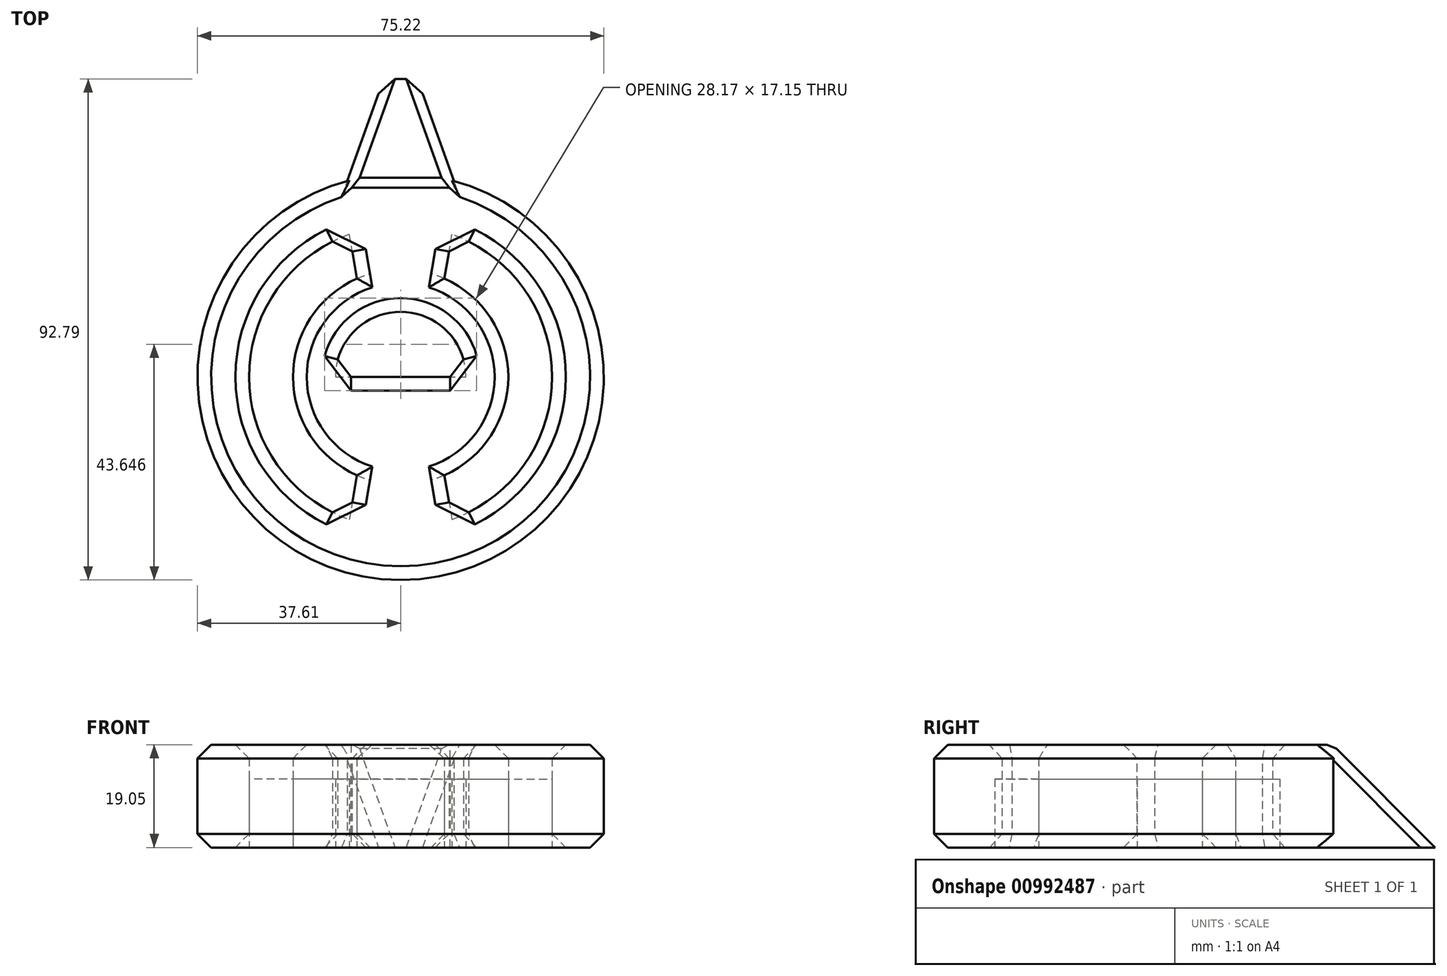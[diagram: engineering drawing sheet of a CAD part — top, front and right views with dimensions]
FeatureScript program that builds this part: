
annotation { "Feature Type Name" : "Feature", "Feature Type Description" : "" }
export const myFeature = defineFeature(function(context is Context, id is Id, definition is map)
    precondition{}
    {
        {
            var Q0;
            Q0=qCreatedBy(makeId("Top.planeOp"),FACE);
            var sketch = newSketch(context, id + "F0", { "sketchPlane" : qUnion([Q0])});
            skLineSegment(sketch, "E0", {"start": v(0, 76.84) * mm, "end": v(0, -76.6) * mm});
            skCircle(sketch, "E1", {"center": v(0, 0) * mm, "radius": 5.51 * mm});
            skCircle(sketch, "E2", {"center": v(0, 0) * mm, "radius": 12.07 * mm});
            skCircle(sketch, "E3", {"center": v(0, 0) * mm, "radius": 37.6 * mm});
            skCircle(sketch, "E4", {"center": v(0, 0) * mm, "radius": 28.06 * mm});
            skCircle(sketch, "E5", {"center": v(0, 0) * mm, "radius": 19.94 * mm});
            skLineSegment(sketch, "E6", {"start": v(-8.1, 18.22) * mm, "end": v(-9.51, 26.4) * mm});
            skLineSegment(sketch, "E7", {"start": v(-76.36, 0) * mm, "end": v(76.42, 0) * mm});
            skLineSegment(sketch, "E8.MirrorCS", {"start": v(-8.1, -18.22) * mm, "end": v(-9.51, -26.4) * mm});
            skLineSegment(sketch, "E9.MirrorCS", {"start": v(8.1, 18.22) * mm, "end": v(9.51, 26.4) * mm});
            skLineSegment(sketch, "E10.MirrorCS", {"start": v(8.1, -18.22) * mm, "end": v(9.51, -26.4) * mm});
            skLineSegment(sketch, "E11", {"start": v(-9.86, 36.3) * mm, "end": v(-3.1, 55.18) * mm});
            skLineSegment(sketch, "E12", {"start": v(-3.1, 55.18) * mm, "end": v(0, 55.18) * mm});
            skLineSegment(sketch, "E13.MirrorCS", {"start": v(9.86, 36.3) * mm, "end": v(3.1, 55.18) * mm});
            skLineSegment(sketch, "E14.MirrorCS", {"start": v(3.1, 55.18) * mm, "end": v(0, 55.18) * mm});
            skSolve(sketch);
        }
        {
            var Q0;
            {var subQ0=sQuery(id+"F0.wireOp",EDGE,"E7");var subQ1=sQuery(id+"F0.wireOp",EDGE,"E0");var subQ2=makeQuery(id+"F0.imprint","INTERSECT",VERTEX,{"derivedFrom":[subQ1,subQ0]});Q0=makeQuery(id+"F0.imprint","IMPRINT",FACE,{"disambiguationData":[TD([[makeQuery(id+"F0.imprint","IMPRINT",EDGE,{"disambiguationData":[TD([[subQ2,-1.0]])],"derivedFrom":subQ1}),1.0]])]});}
            var Q1;
            {var subQ0=sQuery(id+"F0.wireOp",EDGE,"E7");var subQ1=sQuery(id+"F0.wireOp",EDGE,"E0");var subQ2=makeQuery(id+"F0.imprint","INTERSECT",VERTEX,{"derivedFrom":[subQ1,subQ0]});Q1=makeQuery(id+"F0.imprint","IMPRINT",FACE,{"disambiguationData":[TD([[makeQuery(id+"F0.imprint","IMPRINT",EDGE,{"disambiguationData":[TD([[subQ2,-1.0]])],"derivedFrom":subQ1}),-1.0]])]});}
            var Q2;
            {var subQ0=sQuery(id+"F0.wireOp",EDGE,"E1");var subQ1=sQuery(id+"F0.wireOp",EDGE,"E0");var subQ2=makeQuery(id+"F0.imprint","INTERSECT",VERTEX,{"disambiguationData":[OD(0.0)],"derivedFrom":[subQ1,subQ0]});Q2=makeQuery(id+"F0.imprint","IMPRINT",FACE,{"disambiguationData":[TD([[makeQuery(id+"F0.imprint","IMPRINT",EDGE,{"disambiguationData":[TD([[subQ2,-1.0]])],"derivedFrom":subQ1}),-1.0]])]});}
            var Q3;
            {var subQ0=sQuery(id+"F0.wireOp",EDGE,"E1");var subQ1=sQuery(id+"F0.wireOp",EDGE,"E0");var subQ2=makeQuery(id+"F0.imprint","INTERSECT",VERTEX,{"disambiguationData":[OD(0.0)],"derivedFrom":[subQ1,subQ0]});Q3=makeQuery(id+"F0.imprint","IMPRINT",FACE,{"disambiguationData":[TD([[makeQuery(id+"F0.imprint","IMPRINT",EDGE,{"disambiguationData":[TD([[subQ2,-1.0]])],"derivedFrom":subQ1}),1.0]])]});}
            var Q4;
            {var subQ0=sQuery(id+"F0.wireOp",EDGE,"E5");var subQ2=sQuery(id+"F0.wireOp",EDGE,"E0");var subQ3=makeQuery(id+"F0.imprint","INTERSECT",VERTEX,{"disambiguationData":[OD(0.0)],"derivedFrom":[subQ2,subQ0]});Q4=makeQuery(id+"F0.imprint","IMPRINT",FACE,{"disambiguationData":[TD([[makeQuery(id+"F0.imprint","IMPRINT",EDGE,{"disambiguationData":[TD([[subQ3,-1.0]])],"derivedFrom":subQ2}),-1.0]])]});}
            var Q5;
            {var subQ4=sQuery(id+"F0.wireOp",EDGE,"E2");var subQ5=sQuery(id+"F0.wireOp",EDGE,"E0");var subQ6=makeQuery(id+"F0.imprint","INTERSECT",VERTEX,{"disambiguationData":[OD(1.0)],"derivedFrom":[subQ5,subQ4]});Q5=makeQuery(id+"F0.imprint","IMPRINT",FACE,{"disambiguationData":[TD([[makeQuery(id+"F0.imprint","IMPRINT",EDGE,{"disambiguationData":[TD([[subQ6,-1.0]])],"derivedFrom":subQ5}),-1.0]])]});}
            var Q6;
            {var subQ4=sQuery(id+"F0.wireOp",EDGE,"E2");var subQ5=sQuery(id+"F0.wireOp",EDGE,"E0");var subQ6=makeQuery(id+"F0.imprint","INTERSECT",VERTEX,{"disambiguationData":[OD(1.0)],"derivedFrom":[subQ5,subQ4]});Q6=makeQuery(id+"F0.imprint","IMPRINT",FACE,{"disambiguationData":[TD([[makeQuery(id+"F0.imprint","IMPRINT",EDGE,{"disambiguationData":[TD([[subQ6,-1.0]])],"derivedFrom":subQ5}),1.0]])]});}
            var Q7;
            {var subQ0=sQuery(id+"F0.wireOp",EDGE,"E5");var subQ2=sQuery(id+"F0.wireOp",EDGE,"E0");var subQ3=makeQuery(id+"F0.imprint","INTERSECT",VERTEX,{"disambiguationData":[OD(0.0)],"derivedFrom":[subQ2,subQ0]});Q7=makeQuery(id+"F0.imprint","IMPRINT",FACE,{"disambiguationData":[TD([[makeQuery(id+"F0.imprint","IMPRINT",EDGE,{"disambiguationData":[TD([[subQ3,-1.0]])],"derivedFrom":subQ2}),1.0]])]});}
            var Q8;
            {var subQ2=sQuery(id+"F0.wireOp",EDGE,"E0");var subQ4=sQuery(id+"F0.wireOp",EDGE,"E3");var subQ8=makeQuery(id+"F0.imprint","INTERSECT",VERTEX,{"disambiguationData":[OD(1.0)],"derivedFrom":[subQ2,subQ4]});Q8=makeQuery(id+"F0.imprint","IMPRINT",FACE,{"disambiguationData":[TD([[makeQuery(id+"F0.imprint","IMPRINT",EDGE,{"disambiguationData":[TD([[subQ8,-1.0]])],"derivedFrom":subQ2}),-1.0]])]});}
            var Q9;
            {var subQ4=sQuery(id+"F0.wireOp",EDGE,"E3");var subQ5=sQuery(id+"F0.wireOp",EDGE,"E0");var subQ6=makeQuery(id+"F0.imprint","INTERSECT",VERTEX,{"disambiguationData":[OD(0.0)],"derivedFrom":[subQ5,subQ4]});Q9=makeQuery(id+"F0.imprint","IMPRINT",FACE,{"disambiguationData":[TD([[makeQuery(id+"F0.imprint","IMPRINT",EDGE,{"disambiguationData":[TD([[subQ6,1.0]])],"derivedFrom":subQ5}),-1.0]])]});}
            var Q10;
            {var subQ4=sQuery(id+"F0.wireOp",EDGE,"E3");var subQ5=sQuery(id+"F0.wireOp",EDGE,"E0");var subQ6=makeQuery(id+"F0.imprint","INTERSECT",VERTEX,{"disambiguationData":[OD(0.0)],"derivedFrom":[subQ5,subQ4]});Q10=makeQuery(id+"F0.imprint","IMPRINT",FACE,{"disambiguationData":[TD([[makeQuery(id+"F0.imprint","IMPRINT",EDGE,{"disambiguationData":[TD([[subQ6,1.0]])],"derivedFrom":subQ5}),1.0]])]});}
            var Q11;
            {var subQ5=sQuery(id+"F0.wireOp",EDGE,"E10.MirrorCS");Q11=makeQuery(id+"F0.imprint","IMPRINT",FACE,{"disambiguationData":[TD([[makeQuery(id+"F0.imprint","IMPRINT",EDGE,{"derivedFrom":subQ5}),-1.0]])]});}
            var Q12;
            {var subQ5=sQuery(id+"F0.wireOp",EDGE,"E8.MirrorCS");Q12=makeQuery(id+"F0.imprint","IMPRINT",FACE,{"disambiguationData":[TD([[makeQuery(id+"F0.imprint","IMPRINT",EDGE,{"derivedFrom":subQ5}),1.0]])]});}
            var Q13;
            {var subQ4=sQuery(id+"F0.wireOp",EDGE,"E3");var subQ6=sQuery(id+"F0.wireOp",EDGE,"E0");var subQ7=makeQuery(id+"F0.imprint","INTERSECT",VERTEX,{"disambiguationData":[OD(1.0)],"derivedFrom":[subQ6,subQ4]});Q13=makeQuery(id+"F0.imprint","IMPRINT",FACE,{"disambiguationData":[TD([[makeQuery(id+"F0.imprint","IMPRINT",EDGE,{"disambiguationData":[TD([[subQ7,-1.0]])],"derivedFrom":subQ6}),1.0]])]});}
            var Q14;
            {var subQ5=sQuery(id+"F0.wireOp",EDGE,"E9.MirrorCS");Q14=makeQuery(id+"F0.imprint","IMPRINT",FACE,{"disambiguationData":[TD([[makeQuery(id+"F0.imprint","IMPRINT",EDGE,{"derivedFrom":subQ5}),1.0]])]});}
            var Q15;
            {var subQ5=sQuery(id+"F0.wireOp",EDGE,"E6");Q15=makeQuery(id+"F0.imprint","IMPRINT",FACE,{"disambiguationData":[TD([[makeQuery(id+"F0.imprint","IMPRINT",EDGE,{"derivedFrom":subQ5}),-1.0]])]});}
            extrude(context, id + "F1", {"entities" : qUnion([Q0, Q1, Q2, Q3, Q4, Q5, Q6, Q7, Q8, Q9, Q10, Q11, Q12, Q13, Q14, Q15]), "depth" : 19.05 * mm, "offsetDistance" : 25.4 * mm});
        }
        {
            var Q0;
            {var subQ0=sQuery(id+"F0.wireOp",EDGE,"E6");Q0=makeQuery(id+"F0.imprint","IMPRINT",FACE,{"disambiguationData":[TD([[makeQuery(id+"F0.imprint","IMPRINT",EDGE,{"derivedFrom":subQ0}),1.0]])]});}
            var Q1;
            {var subQ0=sQuery(id+"F0.wireOp",EDGE,"E8.MirrorCS");Q1=makeQuery(id+"F0.imprint","IMPRINT",FACE,{"disambiguationData":[TD([[makeQuery(id+"F0.imprint","IMPRINT",EDGE,{"derivedFrom":subQ0}),-1.0]])]});}
            var Q2;
            {var subQ0=sQuery(id+"F0.wireOp",EDGE,"E2");var subQ1=sQuery(id+"F0.wireOp",EDGE,"E0");var subQ2=makeQuery(id+"F0.imprint","INTERSECT",VERTEX,{"disambiguationData":[OD(0.0)],"derivedFrom":[subQ1,subQ0]});Q2=makeQuery(id+"F0.imprint","IMPRINT",FACE,{"disambiguationData":[TD([[makeQuery(id+"F0.imprint","IMPRINT",EDGE,{"disambiguationData":[TD([[subQ2,-1.0]])],"derivedFrom":subQ1}),-1.0]])]});}
            var Q3;
            {var subQ0=sQuery(id+"F0.wireOp",EDGE,"E2");var subQ1=sQuery(id+"F0.wireOp",EDGE,"E0");var subQ2=makeQuery(id+"F0.imprint","INTERSECT",VERTEX,{"disambiguationData":[OD(0.0)],"derivedFrom":[subQ1,subQ0]});Q3=makeQuery(id+"F0.imprint","IMPRINT",FACE,{"disambiguationData":[TD([[makeQuery(id+"F0.imprint","IMPRINT",EDGE,{"disambiguationData":[TD([[subQ2,-1.0]])],"derivedFrom":subQ1}),1.0]])]});}
            var Q4;
            {var subQ0=sQuery(id+"F0.wireOp",EDGE,"E1");var subQ1=sQuery(id+"F0.wireOp",EDGE,"E0");var subQ2=makeQuery(id+"F0.imprint","INTERSECT",VERTEX,{"disambiguationData":[OD(1.0)],"derivedFrom":[subQ1,subQ0]});Q4=makeQuery(id+"F0.imprint","IMPRINT",FACE,{"disambiguationData":[TD([[makeQuery(id+"F0.imprint","IMPRINT",EDGE,{"disambiguationData":[TD([[subQ2,-1.0]])],"derivedFrom":subQ1}),1.0]])]});}
            var Q5;
            {var subQ0=sQuery(id+"F0.wireOp",EDGE,"E1");var subQ1=sQuery(id+"F0.wireOp",EDGE,"E0");var subQ2=makeQuery(id+"F0.imprint","INTERSECT",VERTEX,{"disambiguationData":[OD(1.0)],"derivedFrom":[subQ1,subQ0]});Q5=makeQuery(id+"F0.imprint","IMPRINT",FACE,{"disambiguationData":[TD([[makeQuery(id+"F0.imprint","IMPRINT",EDGE,{"disambiguationData":[TD([[subQ2,-1.0]])],"derivedFrom":subQ1}),-1.0]])]});}
            var Q6;
            {var subQ0=sQuery(id+"F0.wireOp",EDGE,"E9.MirrorCS");Q6=makeQuery(id+"F0.imprint","IMPRINT",FACE,{"disambiguationData":[TD([[makeQuery(id+"F0.imprint","IMPRINT",EDGE,{"derivedFrom":subQ0}),-1.0]])]});}
            var Q7;
            {var subQ0=sQuery(id+"F0.wireOp",EDGE,"E10.MirrorCS");Q7=makeQuery(id+"F0.imprint","IMPRINT",FACE,{"disambiguationData":[TD([[makeQuery(id+"F0.imprint","IMPRINT",EDGE,{"derivedFrom":subQ0}),1.0]])]});}
            extrude(context, id + "F2", {"entities" : qUnion([Q0, Q1, Q2, Q3, Q4, Q5, Q6, Q7]), "depth" : 12.7 * mm, "offsetDistance" : 25.4 * mm});
        }
        {
            var Q0;
            {var subQ4=sQuery(id+"F0.wireOp",EDGE,"E11");Q0=makeQuery(id+"F0.imprint","IMPRINT",FACE,{"disambiguationData":[TD([[makeQuery(id+"F0.imprint","IMPRINT",EDGE,{"derivedFrom":subQ4}),-1.0]])]});}
            var Q1;
            {var subQ4=sQuery(id+"F0.wireOp",EDGE,"E13.MirrorCS");Q1=makeQuery(id+"F0.imprint","IMPRINT",FACE,{"disambiguationData":[TD([[makeQuery(id+"F0.imprint","IMPRINT",EDGE,{"derivedFrom":subQ4}),1.0]])]});}
            extrude(context, id + "F3", {"entities" : qUnion([Q0, Q1]), "operationType" : NewBodyOperationType.ADD, "depth" : 19.05 * mm, "offsetDistance" : 25.4 * mm});
        }
        {
            var Q0;
            Q0=makeQuery(id+"F3.opExtrude","CAP_EDGE",EDGE,{"disambiguationData":[OSD([sQuery(id+"F0.wireOp",EDGE,"E12"),sQuery(id+"F0.wireOp",EDGE,"E14.MirrorCS")])],"isStart":false});
            chamfer(context, id + "F4", {"entities" : qUnion([Q0]), "width" : 19.05 * mm, "tangentPropagation" : true});
        }
        {
            var Q0;
            Q0=makeQuery(id+"F1.opExtrude","CAP_FACE",FACE,{"disambiguationData":[OSD([sQuery(id+"F0.wireOp",EDGE,"E1")])],"isStart":false});
            var Q1;
            Q1=makeQuery(id+"F1.opExtrude","SWEPT_FACE",FACE,{"disambiguationData":[OSD([sQuery(id+"F0.wireOp",EDGE,"E2")])]});
            var Q2;
            {var subQ0=sQuery(id+"F0.wireOp",EDGE,"E4");Q2=makeQuery(id+"F1.opExtrude","SWEPT_FACE",FACE,{"disambiguationData":[OSD([subQ0]),TDD([makeQuery(id+"F0.imprint","IMPRINT",EDGE,{"disambiguationData":[TD([[makeQuery(id+"F0.imprint","INTERSECT",VERTEX,{"derivedFrom":[subQ0,sQuery(id+"F0.wireOp",EDGE,"E9.MirrorCS")]}),1.0]])],"derivedFrom":subQ0}),makeQuery(id+"F0.imprint","IMPRINT",EDGE,{"disambiguationData":[TD([[makeQuery(id+"F0.imprint","INTERSECT",VERTEX,{"derivedFrom":[subQ0,sQuery(id+"F0.wireOp",EDGE,"E10.MirrorCS")]}),-1.0]])],"derivedFrom":subQ0})])]});}
            var Q3;
            {var subQ0=sQuery(id+"F0.wireOp",EDGE,"E4");Q3=makeQuery(id+"F1.opExtrude","SWEPT_FACE",FACE,{"disambiguationData":[OSD([subQ0]),TDD([makeQuery(id+"F0.imprint","IMPRINT",EDGE,{"disambiguationData":[TD([[makeQuery(id+"F0.imprint","INTERSECT",VERTEX,{"derivedFrom":[subQ0,sQuery(id+"F0.wireOp",EDGE,"E6")]}),-1.0]])],"derivedFrom":subQ0}),makeQuery(id+"F0.imprint","IMPRINT",EDGE,{"disambiguationData":[TD([[makeQuery(id+"F0.imprint","INTERSECT",VERTEX,{"derivedFrom":[subQ0,sQuery(id+"F0.wireOp",EDGE,"E8.MirrorCS")]}),1.0]])],"derivedFrom":subQ0})])]});}
            var Q4;
            {var subQ0=sQuery(id+"F0.wireOp",EDGE,"E5");Q4=makeQuery(id+"F1.opExtrude","CAP_EDGE",EDGE,{"disambiguationData":[OSD([subQ0]),TDD([makeQuery(id+"F0.imprint","IMPRINT",EDGE,{"disambiguationData":[TD([[makeQuery(id+"F0.imprint","INTERSECT",VERTEX,{"derivedFrom":[subQ0,sQuery(id+"F0.wireOp",EDGE,"E6")]}),-1.0]])],"derivedFrom":subQ0}),makeQuery(id+"F0.imprint","IMPRINT",EDGE,{"disambiguationData":[TD([[makeQuery(id+"F0.imprint","INTERSECT",VERTEX,{"derivedFrom":[subQ0,sQuery(id+"F0.wireOp",EDGE,"E8.MirrorCS")]}),1.0]])],"derivedFrom":subQ0})])],"isStart":false});}
            var Q5;
            {var subQ0=sQuery(id+"F0.wireOp",EDGE,"E5");Q5=makeQuery(id+"F1.opExtrude","CAP_EDGE",EDGE,{"disambiguationData":[OSD([subQ0]),TDD([makeQuery(id+"F0.imprint","IMPRINT",EDGE,{"disambiguationData":[TD([[makeQuery(id+"F0.imprint","INTERSECT",VERTEX,{"derivedFrom":[subQ0,sQuery(id+"F0.wireOp",EDGE,"E9.MirrorCS")]}),1.0]])],"derivedFrom":subQ0}),makeQuery(id+"F0.imprint","IMPRINT",EDGE,{"disambiguationData":[TD([[makeQuery(id+"F0.imprint","INTERSECT",VERTEX,{"derivedFrom":[subQ0,sQuery(id+"F0.wireOp",EDGE,"E10.MirrorCS")]}),-1.0]])],"derivedFrom":subQ0})])],"isStart":false});}
            var Q6;
            Q6=makeQuery(id+"F1.opExtrude","CAP_EDGE",EDGE,{"disambiguationData":[OSD([sQuery(id+"F0.wireOp",EDGE,"E3")])],"isStart":false});
            var Q7;
            Q7=makeQuery(id+"F1.opExtrude","CAP_EDGE",EDGE,{"disambiguationData":[OSD([sQuery(id+"F0.wireOp",EDGE,"E3")])],"isStart":true});
            chamfer(context, id + "F5", {"entities" : qUnion([Q0, Q1, Q2, Q3, Q4, Q5, Q6, Q7]), "width" : 2.54 * mm, "tangentPropagation" : true});
        }
        {
            var Q0;
            {var subQ0=sQuery(id+"F0.wireOp",EDGE,"E14.MirrorCS");var subQ1=sQuery(id+"F0.wireOp",EDGE,"E12");var subQ2=sQuery(id+"F0.wireOp",EDGE,"E3");Q0=makeQuery(id+"F4.opChamfer","BLEND_EDGE",EDGE,{"blendedFrom":[makeQuery(id+"F3.opExtrude","CAP_EDGE",EDGE,{"disambiguationData":[OSD([subQ1,subQ0])],"isStart":false}),makeQuery(id+"F3.boolean.opBoolean","MERGE",FACE,{"derivedFrom":[makeQuery(id+"F1.opExtrude","CAP_FACE",FACE,{"disambiguationData":[OSD([sQuery(id+"F0.wireOp",EDGE,"E2"),subQ2,sQuery(id+"F0.wireOp",EDGE,"E4"),sQuery(id+"F0.wireOp",EDGE,"E5"),sQuery(id+"F0.wireOp",EDGE,"E6"),sQuery(id+"F0.wireOp",EDGE,"E8.MirrorCS"),sQuery(id+"F0.wireOp",EDGE,"E9.MirrorCS"),sQuery(id+"F0.wireOp",EDGE,"E10.MirrorCS")])],"isStart":false}),makeQuery(id+"F3.opExtrude","CAP_FACE",FACE,{"disambiguationData":[OSD([subQ2,sQuery(id+"F0.wireOp",EDGE,"E11"),subQ1,sQuery(id+"F0.wireOp",EDGE,"E13.MirrorCS"),subQ0])],"isStart":false})]})],"blendedInto":[makeQuery(id+"F3.boolean.opBoolean","MERGE",FACE,{"derivedFrom":[makeQuery(id+"F1.opExtrude","CAP_FACE",FACE,{"disambiguationData":[OSD([sQuery(id+"F0.wireOp",EDGE,"E2"),subQ2,sQuery(id+"F0.wireOp",EDGE,"E4"),sQuery(id+"F0.wireOp",EDGE,"E5"),sQuery(id+"F0.wireOp",EDGE,"E6"),sQuery(id+"F0.wireOp",EDGE,"E8.MirrorCS"),sQuery(id+"F0.wireOp",EDGE,"E9.MirrorCS"),sQuery(id+"F0.wireOp",EDGE,"E10.MirrorCS")])],"isStart":false}),makeQuery(id+"F3.opExtrude","CAP_FACE",FACE,{"disambiguationData":[OSD([subQ2,sQuery(id+"F0.wireOp",EDGE,"E11"),subQ1,sQuery(id+"F0.wireOp",EDGE,"E13.MirrorCS"),subQ0])],"isStart":false})]})]});}
            chamfer(context, id + "F6", {"entities" : qUnion([Q0]), "width" : 2.54 * mm, "tangentPropagation" : true});
        }
        {
            var Q0;
            Q0=makeQuery(id+"F4.opChamfer","BLEND_EDGE",EDGE,{"blendedFrom":[makeQuery(id+"F3.opExtrude","CAP_EDGE",EDGE,{"disambiguationData":[OSD([sQuery(id+"F0.wireOp",EDGE,"E12"),sQuery(id+"F0.wireOp",EDGE,"E14.MirrorCS")])],"isStart":false}),makeQuery(id+"F3.opExtrude","SWEPT_FACE",FACE,{"disambiguationData":[OSD([sQuery(id+"F0.wireOp",EDGE,"E11")])]})],"blendedInto":[makeQuery(id+"F3.opExtrude","SWEPT_FACE",FACE,{"disambiguationData":[OSD([sQuery(id+"F0.wireOp",EDGE,"E11")])]})]});
            var Q1;
            Q1=makeQuery(id+"F4.opChamfer","BLEND_EDGE",EDGE,{"blendedFrom":[makeQuery(id+"F3.opExtrude","CAP_EDGE",EDGE,{"disambiguationData":[OSD([sQuery(id+"F0.wireOp",EDGE,"E12"),sQuery(id+"F0.wireOp",EDGE,"E14.MirrorCS")])],"isStart":false}),makeQuery(id+"F3.opExtrude","SWEPT_FACE",FACE,{"disambiguationData":[OSD([sQuery(id+"F0.wireOp",EDGE,"E13.MirrorCS")])]})],"blendedInto":[makeQuery(id+"F3.opExtrude","SWEPT_FACE",FACE,{"disambiguationData":[OSD([sQuery(id+"F0.wireOp",EDGE,"E13.MirrorCS")])]})]});
            chamfer(context, id + "F7", {"entities" : qUnion([Q0, Q1]), "width" : 2.54 * mm, "tangentPropagation" : true});
        }
    });
